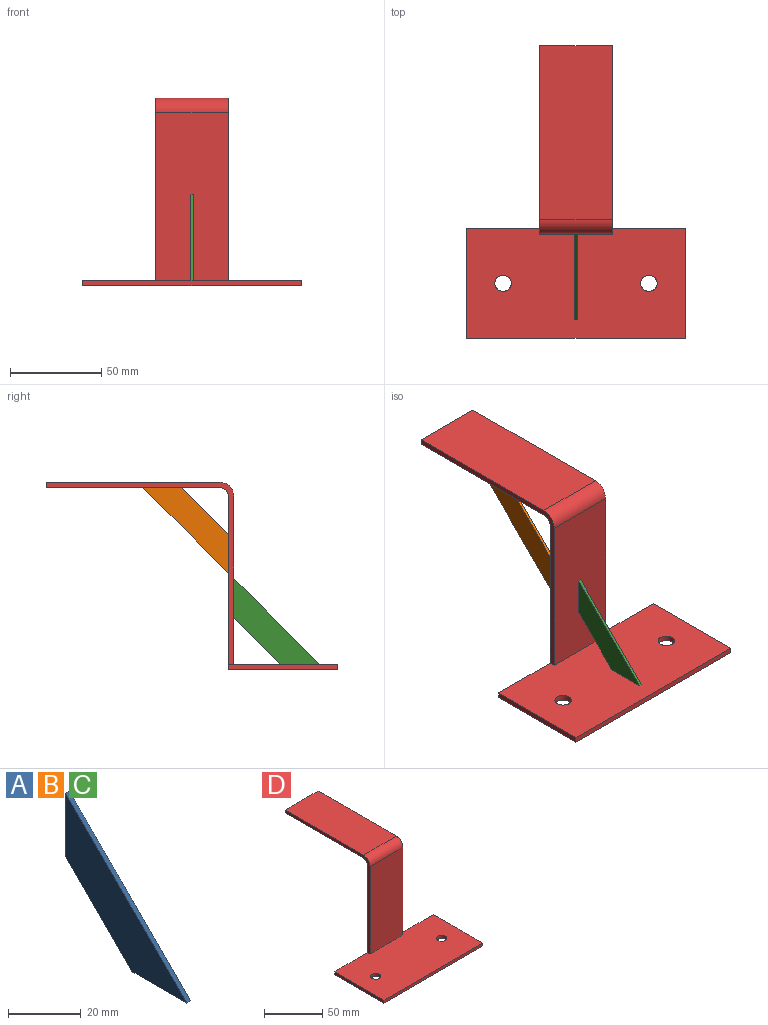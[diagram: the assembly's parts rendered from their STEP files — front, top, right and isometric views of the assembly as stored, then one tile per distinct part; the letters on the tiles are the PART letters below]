
ASSEMBLY  parts=4 mates=6
PART A: 6 faces, bbox 1.5x47x47 mm
  f0: plane 25.79x25.79mm, normal (0,0.71,-0.71), area 54.7mm2, adj f1,f3,f4,f5
  f1: plane 21.21x1.5mm, normal (0,1,0), area 31.8mm2, adj f0,f2,f4,f5
  f2: plane 47x47mm, normal (0,-0.71,0.71), area 99.7mm2, adj f1,f3,f4,f5
  f3: plane 21.21x1.5mm, normal (0,0,-1), area 31.8mm2, adj f0,f2,f4,f5
  f4: plane 47x47mm, normal (1,0,0), area 772mm2, adj f0,f1,f2,f3
  f5: plane 47x47mm, normal (-1,0,0), area 772mm2, adj f0,f1,f2,f3
PART B: same geometry as A
PART C: same geometry as A
PART D: 16 faces, bbox 120x160x103 mm
  f0: plane 60x3mm, normal (1,0,0), area 180mm2, adj f1,f3,f4,f5
  f1: plane 120x95mm, normal (0,1,0), area 4040mm2, adj f0,f2,f4,f5,f7,f12,f13
  f2: plane 60x3mm, normal (-1,0,0), area 180mm2, adj f1,f3,f4,f5
  f3: plane 120x3mm, normal (0,-1,0), area 360mm2, adj f0,f2,f4,f5
  f4: plane 120x60mm, normal (0,0,1), area 6952.8mm2, adj f0,f1,f2,f3,f6,f12,f13,f14
  f5: plane 120x60mm, normal (0,0,-1), area 7072.8mm2, adj f0,f1,f2,f3,f14,f15
  f6: plane 92x40mm, normal (0,-1,0), area 3680mm2, adj f4,f11,f12,f13
  f7: cylinder r=5mm len=40mm, axis (-1,0,0), area 314.2mm2, adj f1,f8,f12,f13
  f8: plane 95x40mm, normal (0,0,-1), area 3800mm2, adj f7,f9,f12,f13
  f9: plane 40x3mm, normal (0,1,0), area 120mm2, adj f8,f10,f12,f13
  f10: plane 95x40mm, normal (0,0,1), area 3800mm2, adj f9,f11,f12,f13
  f11: cylinder r=8mm len=40mm, axis (-1,0,0), area 502.7mm2, adj f6,f10,f12,f13
  f12: plane 103x100mm, normal (1,0,0), area 591.6mm2, adj f1,f4,f6,f7,f8,f9,f10,f11
  f13: plane 103x100mm, normal (-1,0,0), area 591.6mm2, adj f1,f4,f6,f7,f8,f9,f10,f11
  f14: cylinder r=4.5mm len=9mm, axis (0,0,-1), area 84.8mm2, adj f4,f5
  f15: cylinder r=4.5mm len=9mm, axis (0,0,-1), area 84.8mm2, adj f4,f5
PLACE A rot(axis=(1,0,0),180deg) t=(19.25,57,103)mm
PLACE B rot(axis=(1,0,0),180deg) t=(-19.25,57,103)mm
PLACE C at identity
PLACE D at identity fixed
MATE planar A.f4 <-> D.f12  axis (1,0,0) through (20,48.71,81.29)mm
MATE planar A.f3 <-> D.f8  axis (0,0,1) through (19.25,66.39,100)mm
MATE planar B.f5 <-> D.f13  axis (-1,0,0) through (-20,48.71,81.29)mm
MATE planar A.f1 <-> D.f1  axis (0,-1,0) through (19.25,30,63.61)mm
MATE planar B.f1 <-> D.f1  axis (0,-1,0) through (-19.25,30,63.61)mm
MATE planar B.f3 <-> D.f8  axis (0,0,1) through (-19.25,66.39,100)mm
